# Revit family: Faucet-Delta-TRINSIC-TempAssure_17T_Series_H2Okinetic_Tub_and_Shower_Trim
name_source: partatom
category: Plumbing Fixtures
revit_build: Autodesk Revit Architecture 2014 (Build: 20140709_2115(x64)
units: mm (PartAtom-declared; Revit-internal decimal feet)

## types (4) — shared parameters
ADA Compliant = Yes
Actual Valve Water Flow = 0 GPM
CWC R = 0"
Cold Water Connection = 1"
Default Elevation = 3' - 9 1/4"
Depth = 0' - 4 15/16"
Flow Rate = 2.00 gpm @ 80 psi | 7.6 L/min @ 550 kPa maximum water usage

Read more: http://www.deltafaucet.com
HWC R = 0"
Height = 0' - 6 5/8"
Hot Water Connection = 1"
Manufacturer = DELTA
Product Documentation Link = http://www.deltafaucet.com
Product Name = TempAssure 17T Series H2Okinetic Tub and Shower Trim

Read more: http://www.deltafaucet.com
Product Page URL = http://www.deltafaucet.com
Series = Trinsic
URL = http://www.deltafaucet.com
Warranty URL = http://www.deltafaucet.com
Width = 0' - 6 5/8"

## per-type parameters (varying)
| type | Finish |
| T17T459-H2O | Chrome - DELTA - Polished |
| T17T459-CZH2O | Champagne - DELTA - Bronze |
| T17T459-RBH2O | Venetian - DELTA - Bronze |
| T17T459-SSH2O | Steel - DELTA - Brilliance Stainless |

note: column(s) folded — value = type name in every type: Model

## geometry (parser evidence)
native form markers: Blend x12, Sweep x2
no freeform markers — native parametric forms only
